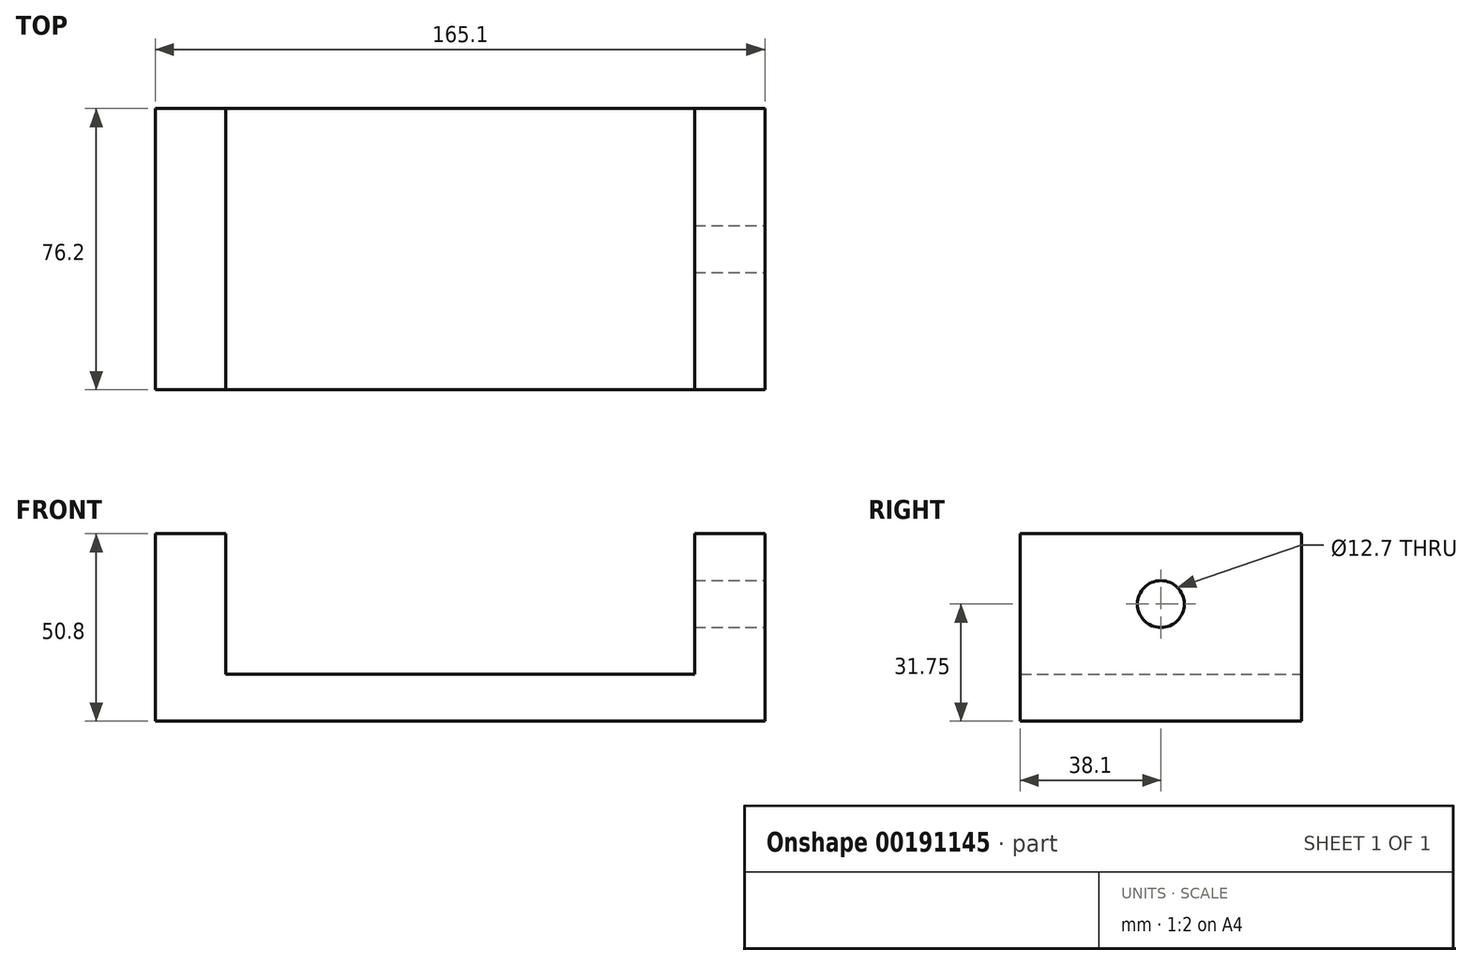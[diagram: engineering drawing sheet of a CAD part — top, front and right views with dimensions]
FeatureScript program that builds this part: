
annotation { "Feature Type Name" : "Feature", "Feature Type Description" : "" }
export const myFeature = defineFeature(function(context is Context, id is Id, definition is map)
    precondition{}
    {
        {
            var Q0;
            Q0=qCreatedBy(makeId("Front.planeOp"),FACE);
            var sketch = newSketch(context, id + "F0", { "sketchPlane" : qUnion([Q0])});
            skLineSegment(sketch, "E0", {"start": v(0, 0) * mm, "end": v(0, 38.1) * mm});
            skLineSegment(sketch, "E1", {"start": v(0, 38.1) * mm, "end": v(19.05, 38.1) * mm});
            skLineSegment(sketch, "E2", {"start": v(19.05, 38.1) * mm, "end": v(19.05, -12.7) * mm});
            skLineSegment(sketch, "E3", {"start": v(19.05, -12.7) * mm, "end": v(-146.05, -12.7) * mm});
            skLineSegment(sketch, "E4", {"start": v(-146.05, -12.7) * mm, "end": v(-146.05, 38.1) * mm});
            skLineSegment(sketch, "E5", {"start": v(-146.05, 38.1) * mm, "end": v(-127, 38.1) * mm});
            skLineSegment(sketch, "E6", {"start": v(-127, 38.1) * mm, "end": v(-127, 0) * mm});
            skLineSegment(sketch, "E7", {"start": v(-127, 0) * mm, "end": v(0, 0) * mm});
            skSolve(sketch);
        }
        {
            var Q0;
            Q0 = qSketchRegion(id + "F0", true);
            extrude(context, id + "F1", {"entities" : qUnion([Q0]), "endBound" : BoundingType.SYMMETRIC, "depth" : 76.2 * mm});
        }
        {
            var Q0;
            Q0=makeQuery(id+"F1.opExtrude","SWEPT_FACE",FACE,{"disambiguationData":[OSD([sQuery(id+"F0.wireOp",EDGE,"E2")])]});
            var sketch = newSketch(context, id + "F2", { "sketchPlane" : qUnion([Q0])});
            skLineSegment(sketch, "E8", {"start": v(-38.1, 0) * mm, "end": v(38.1, 38.1) * mm, "construction": true});
            skPoint(sketch, "E9", {"position": v(0, 19.05) * mm});
            skSolve(sketch);
        }
        {
            var Q0;
            Q0=sQuery(id+"F2.wireOp",VERTEX,"E9");
            var Q1;
            Q1=makeQuery(id+"F1.opExtrude","SWEPT_BODY",BODY,{"disambiguationData":[OSD([sQuery(id+"F0.wireOp",EDGE,"E0"),sQuery(id+"F0.wireOp",EDGE,"E1"),sQuery(id+"F0.wireOp",EDGE,"E2"),sQuery(id+"F0.wireOp",EDGE,"E3"),sQuery(id+"F0.wireOp",EDGE,"E4"),sQuery(id+"F0.wireOp",EDGE,"E5"),sQuery(id+"F0.wireOp",EDGE,"E6"),sQuery(id+"F0.wireOp",EDGE,"E7")])]});
            hole(context, id + "F3", {"style" : HoleStyle.SIMPLE, "endStyle" : HoleEndStyle.BLIND, "holeDiameter" : 12.7 * mm, "holeDepth" : 38.1 * mm, "locations" : qUnion([Q0]), "scope" : qUnion([Q1])});
        }
    });
